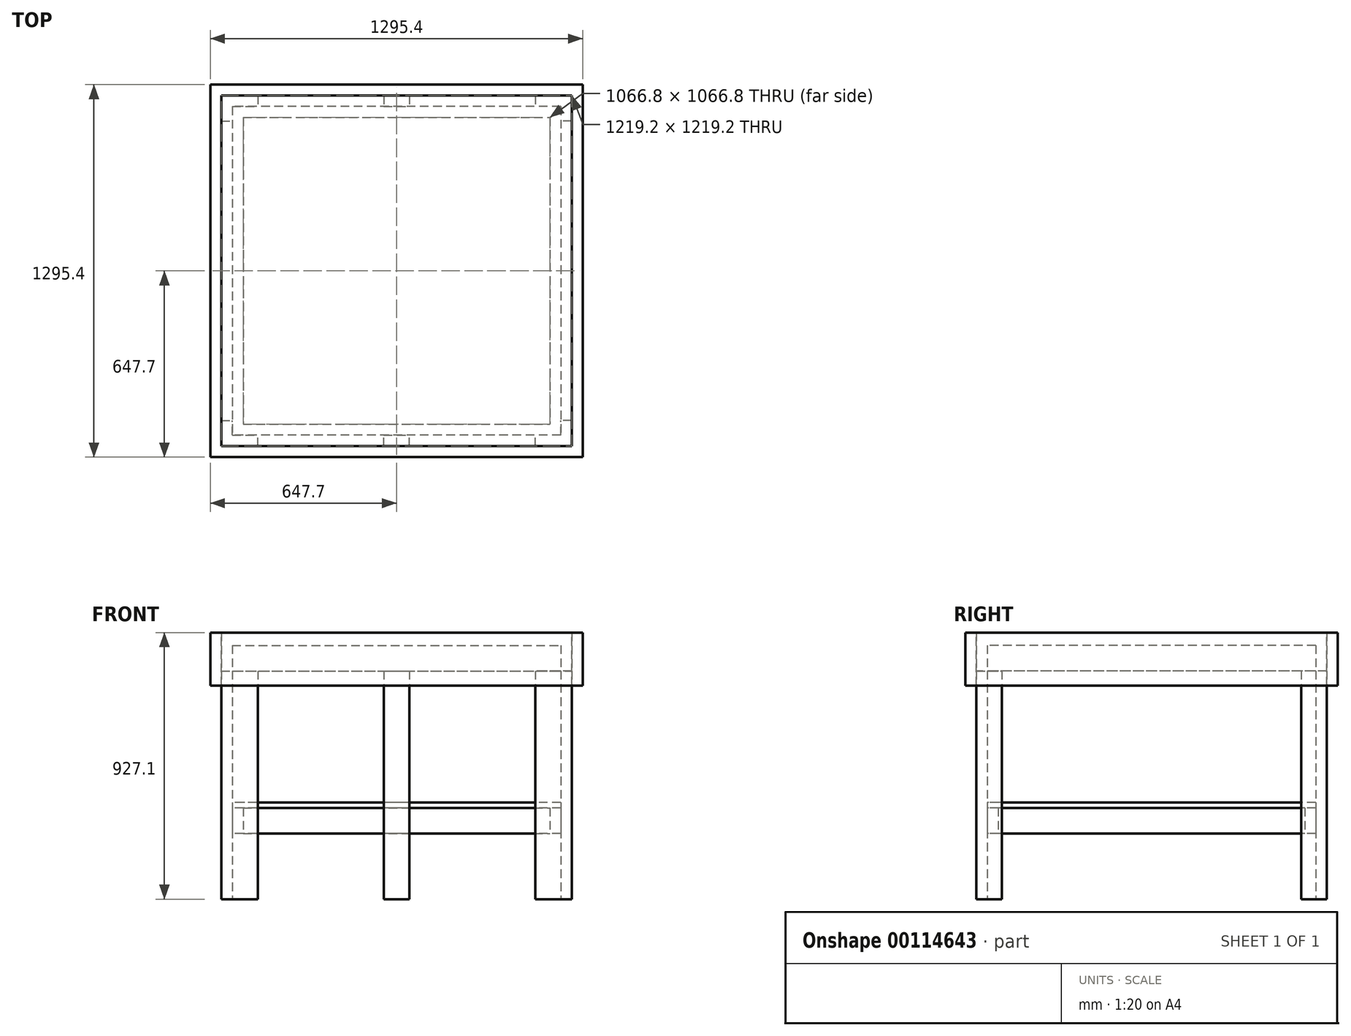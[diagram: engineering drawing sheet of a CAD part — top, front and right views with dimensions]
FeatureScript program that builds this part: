
annotation { "Feature Type Name" : "Feature", "Feature Type Description" : "" }
export const myFeature = defineFeature(function(context is Context, id is Id, definition is map)
    precondition{}
    {
        {
            var Q0;
            Q0=qCreatedBy(makeId("Top.planeOp"),FACE);
            var sketch = newSketch(context, id + "F0", { "sketchPlane" : qUnion([Q0])});
            skLineSegment(sketch, "E0.bottom", {"start": v(0, 0) * mm, "end": v(3124.2, 0) * mm});
            skLineSegment(sketch, "E0.top", {"start": v(0, 889) * mm, "end": v(3124.2, 889) * mm});
            skLineSegment(sketch, "E0.left", {"start": v(0, 0) * mm, "end": v(0, 889) * mm});
            skLineSegment(sketch, "E0.right", {"start": v(3124.2, 0) * mm, "end": v(3124.2, 889) * mm});
            skLineSegment(sketch, "E1.bottom", {"start": v(0, 889) * mm, "end": v(1295.4, 889) * mm});
            skLineSegment(sketch, "E1.top", {"start": v(0, 2184.4) * mm, "end": v(1295.4, 2184.4) * mm});
            skLineSegment(sketch, "E1.left", {"start": v(0, 889) * mm, "end": v(0, 2184.4) * mm});
            skLineSegment(sketch, "E1.right", {"start": v(1295.4, 889) * mm, "end": v(1295.4, 2184.4) * mm});
            skLineSegment(sketch, "E2.bottom", {"start": v(0, 0) * mm, "end": v(1295.4, 0) * mm});
            skLineSegment(sketch, "E2.top", {"start": v(0, -1295.4) * mm, "end": v(1295.4, -1295.4) * mm});
            skLineSegment(sketch, "E2.left", {"start": v(0, 0) * mm, "end": v(0, -1295.4) * mm});
            skLineSegment(sketch, "E2.right", {"start": v(1295.4, 0) * mm, "end": v(1295.4, -1295.4) * mm});
            skLineSegment(sketch, "E3.0", {"start": v(38.1, 927.1) * mm, "end": v(38.1, 2146.3) * mm});
            skLineSegment(sketch, "E3.1", {"start": v(38.1, 927.1) * mm, "end": v(1257.3, 927.1) * mm});
            skLineSegment(sketch, "E3.2", {"start": v(1257.3, 927.1) * mm, "end": v(1257.3, 2146.3) * mm});
            skLineSegment(sketch, "E3.3", {"start": v(38.1, 2146.3) * mm, "end": v(1257.3, 2146.3) * mm});
            skLineSegment(sketch, "E4.0", {"start": v(1257.3, -38.1) * mm, "end": v(1257.3, -1257.3) * mm});
            skLineSegment(sketch, "E4.1", {"start": v(38.1, -38.1) * mm, "end": v(1257.3, -38.1) * mm});
            skLineSegment(sketch, "E4.2", {"start": v(38.1, -38.1) * mm, "end": v(38.1, -1257.3) * mm});
            skLineSegment(sketch, "E4.3", {"start": v(38.1, -1257.3) * mm, "end": v(1257.3, -1257.3) * mm});
            skLineSegment(sketch, "E5.0", {"start": v(38.1, 38.1) * mm, "end": v(38.1, 850.9) * mm});
            skLineSegment(sketch, "E5.1", {"start": v(38.1, 38.1) * mm, "end": v(3086.1, 38.1) * mm});
            skLineSegment(sketch, "E5.2", {"start": v(3086.1, 38.1) * mm, "end": v(3086.1, 850.9) * mm});
            skLineSegment(sketch, "E5.3", {"start": v(38.1, 850.9) * mm, "end": v(3086.1, 850.9) * mm});
            skLineSegment(sketch, "E6", {"start": v(647.7, 2146.3) * mm, "end": v(647.7, 927.1) * mm, "construction": true});
            skLineSegment(sketch, "E7", {"start": v(38.1, 1536.7) * mm, "end": v(1257.3, 1536.7) * mm, "construction": true});
            skLineSegment(sketch, "E8", {"start": v(647.7, -38.1) * mm, "end": v(647.7, -1257.3) * mm, "construction": true});
            skLineSegment(sketch, "E9", {"start": v(38.1, -647.7) * mm, "end": v(1257.3, -647.7) * mm, "construction": true});
            skSolve(sketch);
        }
        {
            var Q0;
            Q0=qCreatedBy(makeId("Top.planeOp"),FACE);
            cPlane(context, id + "F1", {"entities" : qUnion([Q0]), "cplaneType" : CPlaneType.OFFSET, "offset" : 228.6 * mm, "width" : 152.4 * mm, "height" : 152.4 * mm});
        }
        {
            var Q0;
            Q0=qCreatedBy(makeId("Top.planeOp"),FACE);
            var sketch = newSketch(context, id + "F2", { "sketchPlane" : qUnion([Q0])});
            skLineSegment(sketch, "E10.bottom", {"start": v(76.2, 2146.3) * mm, "end": v(165.1, 2146.3) * mm});
            skLineSegment(sketch, "E10.top", {"start": v(76.2, 2108.2) * mm, "end": v(165.1, 2108.2) * mm});
            skLineSegment(sketch, "E10.left", {"start": v(76.2, 2146.3) * mm, "end": v(76.2, 2108.2) * mm});
            skLineSegment(sketch, "E10.right", {"start": v(165.1, 2146.3) * mm, "end": v(165.1, 2108.2) * mm});
            skLineSegment(sketch, "E11.bottom", {"start": v(38.1, 2146.3) * mm, "end": v(76.2, 2146.3) * mm});
            skLineSegment(sketch, "E11.top", {"start": v(38.1, 2057.4) * mm, "end": v(76.2, 2057.4) * mm});
            skLineSegment(sketch, "E11.left", {"start": v(38.1, 2146.3) * mm, "end": v(38.1, 2057.4) * mm});
            skLineSegment(sketch, "E11.right", {"start": v(76.2, 2146.3) * mm, "end": v(76.2, 2057.4) * mm});
            skLineSegment(sketch, "E12.MirrorCS", {"start": v(1257.3, 2146.3) * mm, "end": v(1219.2, 2146.3) * mm});
            skLineSegment(sketch, "E13.MirrorCS", {"start": v(1257.3, 2057.4) * mm, "end": v(1219.2, 2057.4) * mm});
            skLineSegment(sketch, "E14.MirrorCS", {"start": v(1130.3, 2146.3) * mm, "end": v(1130.3, 2108.2) * mm});
            skLineSegment(sketch, "E15.MirrorCS", {"start": v(1219.2, 2146.3) * mm, "end": v(1219.2, 2108.2) * mm});
            skLineSegment(sketch, "E16.MirrorCS", {"start": v(1219.2, 2146.3) * mm, "end": v(1219.2, 2057.4) * mm});
            skLineSegment(sketch, "E17.MirrorCS", {"start": v(1219.2, 2146.3) * mm, "end": v(1130.3, 2146.3) * mm});
            skLineSegment(sketch, "E18.MirrorCS", {"start": v(1219.2, 2108.2) * mm, "end": v(1130.3, 2108.2) * mm});
            skLineSegment(sketch, "E19.MirrorCS", {"start": v(1257.3, 2146.3) * mm, "end": v(1257.3, 2057.4) * mm});
            skLineSegment(sketch, "E20.MirrorCS", {"start": v(1257.3, 927.1) * mm, "end": v(1219.2, 927.1) * mm});
            skLineSegment(sketch, "E21.MirrorCS", {"start": v(76.2, 927.1) * mm, "end": v(76.2, 1016) * mm});
            skLineSegment(sketch, "E22.MirrorCS", {"start": v(38.1, 1016) * mm, "end": v(76.2, 1016) * mm});
            skLineSegment(sketch, "E23.MirrorCS", {"start": v(1130.3, 927.1) * mm, "end": v(1130.3, 965.2) * mm});
            skLineSegment(sketch, "E24.MirrorCS", {"start": v(165.1, 927.1) * mm, "end": v(165.1, 965.2) * mm});
            skLineSegment(sketch, "E25.MirrorCS", {"start": v(38.1, 927.1) * mm, "end": v(76.2, 927.1) * mm});
            skLineSegment(sketch, "E26.MirrorCS", {"start": v(1257.3, 1016) * mm, "end": v(1219.2, 1016) * mm});
            skLineSegment(sketch, "E27.MirrorCS", {"start": v(1219.2, 927.1) * mm, "end": v(1219.2, 965.2) * mm});
            skLineSegment(sketch, "E28.MirrorCS", {"start": v(1219.2, 927.1) * mm, "end": v(1219.2, 1016) * mm});
            skLineSegment(sketch, "E29.MirrorCS", {"start": v(76.2, 927.1) * mm, "end": v(76.2, 965.2) * mm});
            skLineSegment(sketch, "E30.MirrorCS", {"start": v(38.1, 927.1) * mm, "end": v(38.1, 1016) * mm});
            skLineSegment(sketch, "E31.MirrorCS", {"start": v(1257.3, 927.1) * mm, "end": v(1257.3, 1016) * mm});
            skLineSegment(sketch, "E32.MirrorCS", {"start": v(76.2, 927.1) * mm, "end": v(165.1, 927.1) * mm});
            skLineSegment(sketch, "E33.MirrorCS", {"start": v(1219.2, 927.1) * mm, "end": v(1130.3, 927.1) * mm});
            skLineSegment(sketch, "E34.MirrorCS", {"start": v(76.2, 965.2) * mm, "end": v(165.1, 965.2) * mm});
            skLineSegment(sketch, "E35.MirrorCS", {"start": v(1219.2, 965.2) * mm, "end": v(1130.3, 965.2) * mm});
            skLineSegment(sketch, "E36.bottom", {"start": v(603.25, 2146.3) * mm, "end": v(692.15, 2146.3) * mm});
            skLineSegment(sketch, "E36.top", {"start": v(603.25, 2108.2) * mm, "end": v(692.15, 2108.2) * mm});
            skLineSegment(sketch, "E36.left", {"start": v(603.25, 2146.3) * mm, "end": v(603.25, 2108.2) * mm});
            skLineSegment(sketch, "E36.right", {"start": v(692.15, 2146.3) * mm, "end": v(692.15, 2108.2) * mm});
            skPoint(sketch, "E37", {"position": v(647.7, 2146.3) * mm});
            skLineSegment(sketch, "E38.MirrorCS", {"start": v(603.25, 927.1) * mm, "end": v(692.15, 927.1) * mm});
            skLineSegment(sketch, "E39.MirrorCS", {"start": v(603.25, 965.2) * mm, "end": v(692.15, 965.2) * mm});
            skPoint(sketch, "E40.MirrorP", {"position": v(647.7, 927.1) * mm});
            skLineSegment(sketch, "E41.MirrorCS", {"start": v(603.25, 927.1) * mm, "end": v(603.25, 965.2) * mm});
            skLineSegment(sketch, "E42.MirrorCS", {"start": v(692.15, 927.1) * mm, "end": v(692.15, 965.2) * mm});
            skSolve(sketch);
        }
        {
            var Q0;
            Q0 = qSketchRegion(id + "F2", true);
            extrude(context, id + "F3", {"entities" : qUnion([Q0]), "depth" : 793.75 * mm});
        }
        {
            var Q0;
            Q0=qCreatedBy(id+"F1.planeOp",FACE);
            var sketch = newSketch(context, id + "F4", { "sketchPlane" : qUnion([Q0])});
            skLineSegment(sketch, "E43.bottom", {"start": v(114.3, 2108.2) * mm, "end": v(76.2, 2108.2) * mm});
            skLineSegment(sketch, "E43.top", {"start": v(114.3, 965.2) * mm, "end": v(76.2, 965.2) * mm});
            skLineSegment(sketch, "E43.left", {"start": v(114.3, 2108.2) * mm, "end": v(114.3, 965.2) * mm});
            skLineSegment(sketch, "E43.right", {"start": v(76.2, 2108.2) * mm, "end": v(76.2, 965.2) * mm});
            skLineSegment(sketch, "E44.bottom", {"start": v(114.3, 2108.2) * mm, "end": v(1181.1, 2108.2) * mm});
            skLineSegment(sketch, "E44.top", {"start": v(114.3, 2070.1) * mm, "end": v(1181.1, 2070.1) * mm});
            skLineSegment(sketch, "E44.left", {"start": v(114.3, 2108.2) * mm, "end": v(114.3, 2070.1) * mm});
            skLineSegment(sketch, "E44.right", {"start": v(1181.1, 2108.2) * mm, "end": v(1181.1, 2070.1) * mm});
            skLineSegment(sketch, "E45.MirrorCS", {"start": v(1181.1, 965.2) * mm, "end": v(1219.2, 965.2) * mm});
            skLineSegment(sketch, "E46.MirrorCS", {"start": v(1181.1, 2108.2) * mm, "end": v(1219.2, 2108.2) * mm});
            skLineSegment(sketch, "E47.MirrorCS", {"start": v(1181.1, 2108.2) * mm, "end": v(1181.1, 965.2) * mm});
            skLineSegment(sketch, "E48.MirrorCS", {"start": v(1219.2, 2108.2) * mm, "end": v(1219.2, 965.2) * mm});
            skLineSegment(sketch, "E49.MirrorCS", {"start": v(1181.1, 965.2) * mm, "end": v(1181.1, 1003.3) * mm});
            skLineSegment(sketch, "E50.MirrorCS", {"start": v(114.3, 965.2) * mm, "end": v(114.3, 1003.3) * mm});
            skLineSegment(sketch, "E51.MirrorCS", {"start": v(114.3, 1003.3) * mm, "end": v(1181.1, 1003.3) * mm});
            skLineSegment(sketch, "E52.MirrorCS", {"start": v(114.3, 965.2) * mm, "end": v(1181.1, 965.2) * mm});
            skLineSegment(sketch, "E53.bottom", {"start": v(628.65, 2070.1) * mm, "end": v(666.75, 2070.1) * mm});
            skLineSegment(sketch, "E53.top", {"start": v(628.65, 1003.3) * mm, "end": v(666.75, 1003.3) * mm});
            skLineSegment(sketch, "E53.left", {"start": v(628.65, 2070.1) * mm, "end": v(628.65, 1003.3) * mm});
            skLineSegment(sketch, "E53.right", {"start": v(666.75, 2070.1) * mm, "end": v(666.75, 1003.3) * mm});
            skPoint(sketch, "E54", {"position": v(647.7, 2070.1) * mm});
            skSolve(sketch);
        }
        {
            var Q0;
            Q0 = qSketchRegion(id + "F4", true);
            var Q1;
            Q1=makeQuery(id+"F4.imprint","IMPRINT",FACE,{"disambiguationData":[TD([[makeQuery(id+"F4.imprint","IMPRINT",EDGE,{"derivedFrom":sQuery(id+"F4.wireOp",EDGE,"E53.bottom")}),-1.0]])]});
            extrude(context, id + "F5", {"entities" : qUnion([Q0, Q1]), "depth" : 88.9 * mm});
        }
        {
            var Q0;
            Q0=makeQuery(id+"F5.opExtrude","CAP_FACE",FACE,{"disambiguationData":[OSD([sQuery(id+"F4.wireOp",EDGE,"E43.bottom"),sQuery(id+"F4.wireOp",EDGE,"E43.top"),sQuery(id+"F4.wireOp",EDGE,"E43.left"),sQuery(id+"F4.wireOp",EDGE,"E43.right"),sQuery(id+"F4.wireOp",EDGE,"E44.bottom"),sQuery(id+"F4.wireOp",EDGE,"E44.top"),sQuery(id+"F4.wireOp",EDGE,"E45.MirrorCS"),sQuery(id+"F4.wireOp",EDGE,"E46.MirrorCS"),sQuery(id+"F4.wireOp",EDGE,"E47.MirrorCS"),sQuery(id+"F4.wireOp",EDGE,"E48.MirrorCS"),sQuery(id+"F4.wireOp",EDGE,"E51.MirrorCS"),sQuery(id+"F4.wireOp",EDGE,"E52.MirrorCS"),sQuery(id+"F4.wireOp",EDGE,"E53.left"),sQuery(id+"F4.wireOp",EDGE,"E53.right")])],"isStart":false});
            var sketch = newSketch(context, id + "F6", { "sketchPlane" : qUnion([Q0])});
            skLineSegment(sketch, "E55.bottom", {"start": v(76.2, 2108.2) * mm, "end": v(1219.2, 2108.2) * mm});
            skLineSegment(sketch, "E55.top", {"start": v(76.2, 965.2) * mm, "end": v(1219.2, 965.2) * mm});
            skLineSegment(sketch, "E55.left", {"start": v(76.2, 2108.2) * mm, "end": v(76.2, 965.2) * mm});
            skLineSegment(sketch, "E55.right", {"start": v(1219.2, 2108.2) * mm, "end": v(1219.2, 965.2) * mm});
            skSolve(sketch);
        }
        {
            var Q0;
            Q0 = qSketchRegion(id + "F6", true);
            extrude(context, id + "F7", {"entities" : qUnion([Q0]), "depth" : 19.05 * mm});
        }
        {
            var Q0;
            Q0=makeQuery(id+"F3.opExtrude","CAP_FACE",FACE,{"disambiguationData":[OSD([sQuery(id+"F2.wireOp",EDGE,"E21.MirrorCS"),sQuery(id+"F2.wireOp",EDGE,"E22.MirrorCS"),sQuery(id+"F2.wireOp",EDGE,"E24.MirrorCS"),sQuery(id+"F2.wireOp",EDGE,"E25.MirrorCS"),sQuery(id+"F2.wireOp",EDGE,"E30.MirrorCS"),sQuery(id+"F2.wireOp",EDGE,"E32.MirrorCS"),sQuery(id+"F2.wireOp",EDGE,"E34.MirrorCS")])],"isStart":false});
            var sketch = newSketch(context, id + "F8", { "sketchPlane" : qUnion([Q0])});
            skLineSegment(sketch, "E56.bottom", {"start": v(38.1, 2146.3) * mm, "end": v(76.2, 2146.3) * mm});
            skLineSegment(sketch, "E56.top", {"start": v(38.1, 927.1) * mm, "end": v(76.2, 927.1) * mm});
            skLineSegment(sketch, "E56.left", {"start": v(38.1, 2146.3) * mm, "end": v(38.1, 927.1) * mm});
            skLineSegment(sketch, "E56.right", {"start": v(76.2, 2146.3) * mm, "end": v(76.2, 927.1) * mm});
            skLineSegment(sketch, "E57.MirrorCS", {"start": v(1257.3, 927.1) * mm, "end": v(1219.2, 927.1) * mm});
            skLineSegment(sketch, "E58.MirrorCS", {"start": v(1257.3, 2146.3) * mm, "end": v(1219.2, 2146.3) * mm});
            skLineSegment(sketch, "E59.MirrorCS", {"start": v(1219.2, 2146.3) * mm, "end": v(1219.2, 927.1) * mm});
            skLineSegment(sketch, "E60.MirrorCS", {"start": v(1257.3, 2146.3) * mm, "end": v(1257.3, 927.1) * mm});
            skLineSegment(sketch, "E61.bottom", {"start": v(76.2, 2146.3) * mm, "end": v(1219.2, 2146.3) * mm});
            skLineSegment(sketch, "E61.top", {"start": v(76.2, 2108.2) * mm, "end": v(1219.2, 2108.2) * mm});
            skLineSegment(sketch, "E61.left", {"start": v(76.2, 2146.3) * mm, "end": v(76.2, 2108.2) * mm});
            skLineSegment(sketch, "E61.right", {"start": v(1219.2, 2146.3) * mm, "end": v(1219.2, 2108.2) * mm});
            skLineSegment(sketch, "E62.MirrorCS", {"start": v(1219.2, 927.1) * mm, "end": v(1219.2, 965.2) * mm});
            skLineSegment(sketch, "E63.MirrorCS", {"start": v(76.2, 927.1) * mm, "end": v(76.2, 965.2) * mm});
            skLineSegment(sketch, "E64.MirrorCS", {"start": v(76.2, 965.2) * mm, "end": v(1219.2, 965.2) * mm});
            skLineSegment(sketch, "E65.MirrorCS", {"start": v(76.2, 927.1) * mm, "end": v(1219.2, 927.1) * mm});
            skLineSegment(sketch, "E66.bottom", {"start": v(333.37, 2108.2) * mm, "end": v(371.47, 2108.2) * mm});
            skLineSegment(sketch, "E66.top", {"start": v(333.37, 965.2) * mm, "end": v(371.47, 965.2) * mm});
            skLineSegment(sketch, "E66.left", {"start": v(333.37, 2108.2) * mm, "end": v(333.37, 965.2) * mm});
            skLineSegment(sketch, "E66.right", {"start": v(371.47, 2108.2) * mm, "end": v(371.47, 965.2) * mm});
            skLineSegment(sketch, "E67.bottom", {"start": v(923.92, 2108.2) * mm, "end": v(962.02, 2108.2) * mm});
            skLineSegment(sketch, "E67.top", {"start": v(923.92, 965.2) * mm, "end": v(962.02, 965.2) * mm});
            skLineSegment(sketch, "E67.left", {"start": v(923.92, 2108.2) * mm, "end": v(923.92, 965.2) * mm});
            skLineSegment(sketch, "E67.right", {"start": v(962.02, 2108.2) * mm, "end": v(962.02, 965.2) * mm});
            skLineSegment(sketch, "E68.bottom", {"start": v(628.65, 2108.2) * mm, "end": v(666.75, 2108.2) * mm});
            skLineSegment(sketch, "E68.top", {"start": v(628.65, 965.2) * mm, "end": v(666.75, 965.2) * mm});
            skLineSegment(sketch, "E68.left", {"start": v(628.65, 2108.2) * mm, "end": v(628.65, 965.2) * mm});
            skLineSegment(sketch, "E68.right", {"start": v(666.75, 2108.2) * mm, "end": v(666.75, 965.2) * mm});
            skPoint(sketch, "E69", {"position": v(647.7, 2108.2) * mm});
            skSolve(sketch);
        }
        {
            var Q0;
            Q0 = qSketchRegion(id + "F8", true);
            var Q1;
            Q1=makeQuery(id+"F8.imprint","IMPRINT",FACE,{"disambiguationData":[TD([[makeQuery(id+"F8.imprint","IMPRINT",EDGE,{"derivedFrom":sQuery(id+"F8.wireOp",EDGE,"E66.bottom")}),-1.0]])]});
            var Q2;
            Q2=makeQuery(id+"F8.imprint","IMPRINT",FACE,{"disambiguationData":[TD([[makeQuery(id+"F8.imprint","IMPRINT",EDGE,{"derivedFrom":sQuery(id+"F8.wireOp",EDGE,"E68.bottom")}),-1.0]])]});
            var Q3;
            Q3=makeQuery(id+"F8.imprint","IMPRINT",FACE,{"disambiguationData":[TD([[makeQuery(id+"F8.imprint","IMPRINT",EDGE,{"derivedFrom":sQuery(id+"F8.wireOp",EDGE,"E67.bottom")}),-1.0]])]});
            extrude(context, id + "F9", {"entities" : qUnion([Q0, Q1, Q2, Q3]), "depth" : 88.9 * mm});
        }
        {
            var Q0;
            Q0=makeQuery(id+"F9.opExtrude","CAP_FACE",FACE,{"disambiguationData":[OSD([sQuery(id+"F8.wireOp",EDGE,"E56.bottom"),sQuery(id+"F8.wireOp",EDGE,"E56.top"),sQuery(id+"F8.wireOp",EDGE,"E56.left"),sQuery(id+"F8.wireOp",EDGE,"E56.right"),sQuery(id+"F8.wireOp",EDGE,"E57.MirrorCS"),sQuery(id+"F8.wireOp",EDGE,"E58.MirrorCS"),sQuery(id+"F8.wireOp",EDGE,"E59.MirrorCS"),sQuery(id+"F8.wireOp",EDGE,"E60.MirrorCS"),sQuery(id+"F8.wireOp",EDGE,"E61.bottom"),sQuery(id+"F8.wireOp",EDGE,"E61.top"),sQuery(id+"F8.wireOp",EDGE,"E64.MirrorCS"),sQuery(id+"F8.wireOp",EDGE,"E65.MirrorCS"),sQuery(id+"F8.wireOp",EDGE,"E66.left"),sQuery(id+"F8.wireOp",EDGE,"E66.right"),sQuery(id+"F8.wireOp",EDGE,"E67.left"),sQuery(id+"F8.wireOp",EDGE,"E67.right"),sQuery(id+"F8.wireOp",EDGE,"E68.left"),sQuery(id+"F8.wireOp",EDGE,"E68.right")])],"isStart":false});
            var sketch = newSketch(context, id + "F10", { "sketchPlane" : qUnion([Q0])});
            skLineSegment(sketch, "E70.bottom", {"start": v(38.1, 2146.3) * mm, "end": v(1257.3, 2146.3) * mm});
            skLineSegment(sketch, "E70.top", {"start": v(38.1, 927.1) * mm, "end": v(1257.3, 927.1) * mm});
            skLineSegment(sketch, "E70.left", {"start": v(38.1, 2146.3) * mm, "end": v(38.1, 927.1) * mm});
            skLineSegment(sketch, "E70.right", {"start": v(1257.3, 2146.3) * mm, "end": v(1257.3, 927.1) * mm});
            skSolve(sketch);
        }
        {
            var Q0;
            Q0 = qSketchRegion(id + "F10", true);
            extrude(context, id + "F11", {"entities" : qUnion([Q0]), "operationType" : NewBodyOperationType.ADD, "depth" : 44.45 * mm});
        }
        {
            var Q0;
            Q0=makeQuery(id+"F11.opExtrude","CAP_FACE",FACE,{"disambiguationData":[OSD([sQuery(id+"F10.wireOp",EDGE,"E70.bottom"),sQuery(id+"F10.wireOp",EDGE,"E70.top"),sQuery(id+"F10.wireOp",EDGE,"E70.left"),sQuery(id+"F10.wireOp",EDGE,"E70.right")])],"isStart":false});
            var sketch = newSketch(context, id + "F12", { "sketchPlane" : qUnion([Q0])});
            skLineSegment(sketch, "E71.bottom", {"start": v(0, 2184.4) * mm, "end": v(1295.4, 2184.4) * mm});
            skLineSegment(sketch, "E71.top", {"start": v(0, 2146.3) * mm, "end": v(1295.4, 2146.3) * mm});
            skLineSegment(sketch, "E71.left", {"start": v(0, 2184.4) * mm, "end": v(0, 2146.3) * mm});
            skLineSegment(sketch, "E71.right", {"start": v(1295.4, 2184.4) * mm, "end": v(1295.4, 2146.3) * mm});
            skLineSegment(sketch, "E72.bottom", {"start": v(0, 2146.3) * mm, "end": v(38.1, 2146.3) * mm});
            skLineSegment(sketch, "E72.top", {"start": v(0, 927.1) * mm, "end": v(38.1, 927.1) * mm});
            skLineSegment(sketch, "E72.left", {"start": v(0, 2146.3) * mm, "end": v(0, 927.1) * mm});
            skLineSegment(sketch, "E72.right", {"start": v(38.1, 2146.3) * mm, "end": v(38.1, 927.1) * mm});
            skLineSegment(sketch, "E73.MirrorCS", {"start": v(1295.4, 927.1) * mm, "end": v(1257.3, 927.1) * mm});
            skLineSegment(sketch, "E74.MirrorCS", {"start": v(1295.4, 2146.3) * mm, "end": v(1257.3, 2146.3) * mm});
            skLineSegment(sketch, "E75.MirrorCS", {"start": v(1295.4, 2146.3) * mm, "end": v(1295.4, 927.1) * mm});
            skLineSegment(sketch, "E76.MirrorCS", {"start": v(1257.3, 2146.3) * mm, "end": v(1257.3, 927.1) * mm});
            skLineSegment(sketch, "E77.MirrorCS", {"start": v(0, 889) * mm, "end": v(0, 927.1) * mm});
            skLineSegment(sketch, "E78.MirrorCS", {"start": v(1295.4, 889) * mm, "end": v(1295.4, 927.1) * mm});
            skLineSegment(sketch, "E79.MirrorCS", {"start": v(0, 927.1) * mm, "end": v(1295.4, 927.1) * mm});
            skLineSegment(sketch, "E80.MirrorCS", {"start": v(0, 889) * mm, "end": v(1295.4, 889) * mm});
            skSolve(sketch);
        }
        {
            var Q0;
            Q0 = qSketchRegion(id + "F12", true);
            extrude(context, id + "F13", {"entities" : qUnion([Q0]), "oppositeDirection" : true, "depth" : 184.15 * mm});
        }
    });
